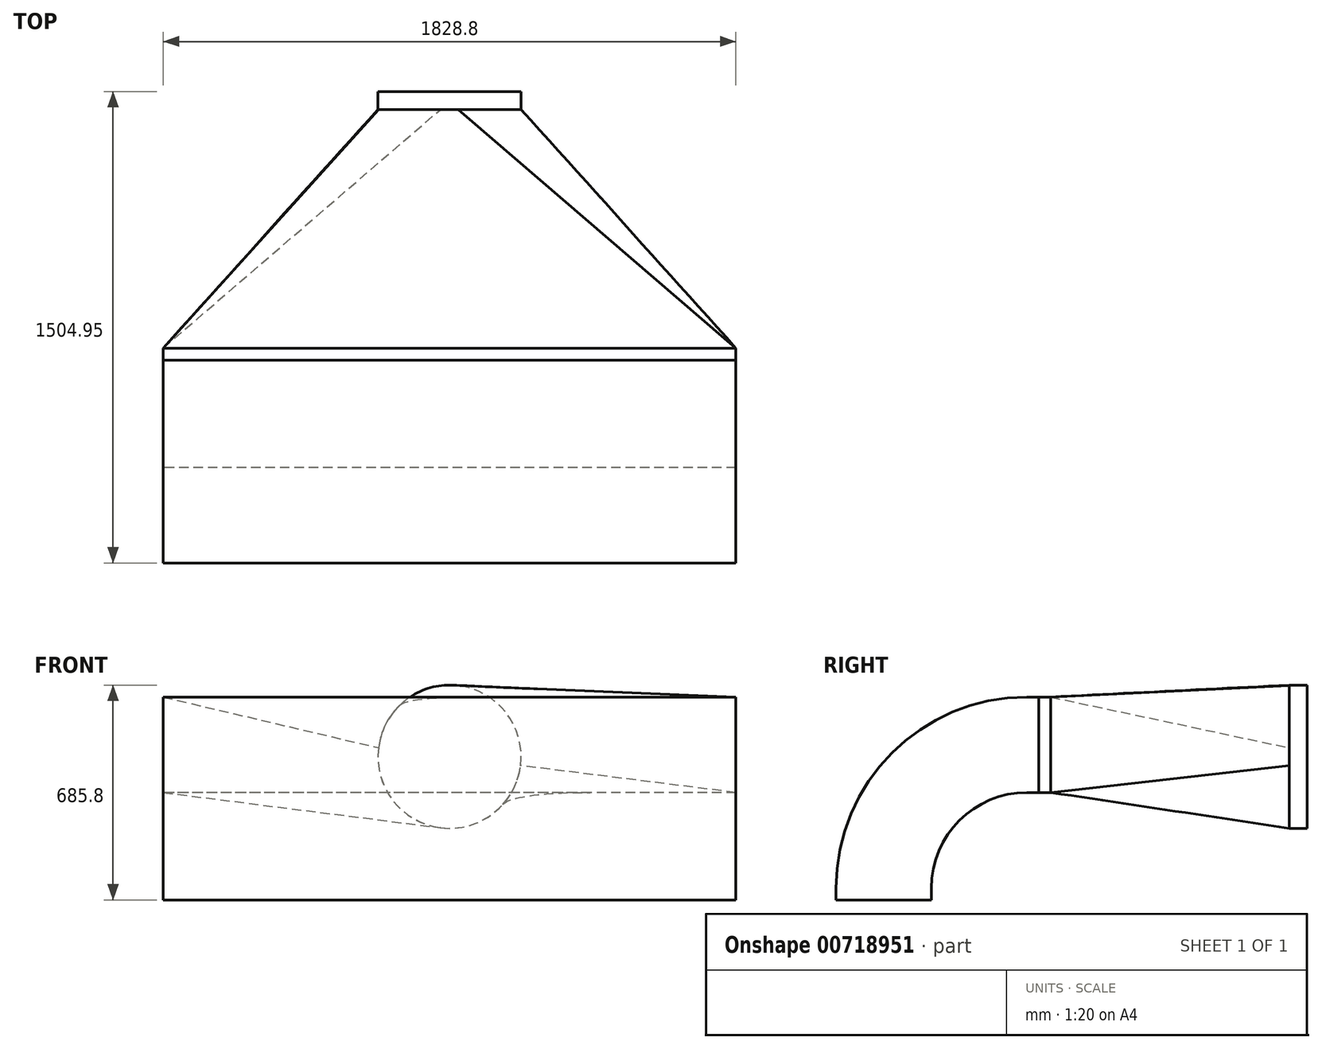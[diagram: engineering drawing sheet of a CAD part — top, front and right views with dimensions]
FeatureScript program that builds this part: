
annotation { "Feature Type Name" : "Feature", "Feature Type Description" : "" }
export const myFeature = defineFeature(function(context is Context, id is Id, definition is map)
    precondition{}
    {
        {
            var Q0;
            Q0=qCreatedBy(makeId("Top.planeOp"),FACE);
            var sketch = newSketch(context, id + "F0", { "sketchPlane" : qUnion([Q0])});
            skLineSegment(sketch, "E0.bottom", {"start": v(914.4, 152.4) * mm, "end": v(-914.4, 152.4) * mm});
            skLineSegment(sketch, "E0.top", {"start": v(914.4, -152.4) * mm, "end": v(-914.4, -152.4) * mm});
            skLineSegment(sketch, "E0.left", {"start": v(914.4, 152.4) * mm, "end": v(914.4, -152.4) * mm});
            skLineSegment(sketch, "E0.right", {"start": v(-914.4, 152.4) * mm, "end": v(-914.4, -152.4) * mm});
            skPoint(sketch, "E0.middle", {"position": v(0, 0) * mm});
            skSolve(sketch);
        }
        {
            var Q0;
            Q0=makeQuery(id+"F0.imprint","IMPRINT",FACE,{"disambiguationData":[TD([[makeQuery(id+"F0.imprint","IMPRINT",EDGE,{"derivedFrom":sQuery(id+"F0.wireOp",EDGE,"E0.bottom")}),1.0]])]});
            extrude(context, id + "F1", {"entities" : qUnion([Q0]), "depth" : 38.1 * mm, "offsetDistance" : 25.4 * mm});
        }
        {
            var Q0;
            Q0=makeQuery(id+"F1.opExtrude","CAP_FACE",FACE,{"disambiguationData":[OSD([sQuery(id+"F0.wireOp",EDGE,"E0.bottom"),sQuery(id+"F0.wireOp",EDGE,"E0.top"),sQuery(id+"F0.wireOp",EDGE,"E0.left"),sQuery(id+"F0.wireOp",EDGE,"E0.right")])],"isStart":false});
            var sketch = newSketch(context, id + "F2", { "sketchPlane" : qUnion([Q0])});
            skLineSegment(sketch, "E1", {"start": v(0, 0) * mm, "end": v(0, 457.2) * mm, "construction": true});
            skPoint(sketch, "E1.endSnap0", {"position": v(0, 152.4) * mm});
            skLineSegment(sketch, "E2", {"start": v(0, 457.2) * mm, "end": v(-206.41, 457.2) * mm});
            skSolve(sketch);
        }
        {
            var Q0;
            Q0=makeQuery(id+"F2.imprint","IMPRINT",FACE,{"disambiguationData":[TD([[makeQuery(id+"F2.imprint","IMPRINT",EDGE,{"derivedFrom":makeQuery(id+"F1.opExtrude","CAP_EDGE",EDGE,{"disambiguationData":[OSD([sQuery(id+"F0.wireOp",EDGE,"E0.bottom")])],"isStart":false})}),1.0]])]});
            var Q1;
            Q1=sQuery(id+"F2.wireOp",EDGE,"E2");
            revolve(context, id + "F3", {"operationType" : NewBodyOperationType.ADD, "surfaceOperationType" : NewSurfaceOperationType.NEW, "entities" : qUnion([Q0]), "axis" : qUnion([Q1]), "revolveType" : RevolveType.ONE_DIRECTION, "angle" : 90 * degree});
        }
        {
            var Q0;
            Q0=makeQuery(id+"F3.opRevolve","CAP_FACE",FACE,{"disambiguationData":[OSD([sQuery(id+"F0.wireOp",EDGE,"E0.bottom"),sQuery(id+"F0.wireOp",EDGE,"E0.top"),sQuery(id+"F0.wireOp",EDGE,"E0.left"),sQuery(id+"F0.wireOp",EDGE,"E0.right")])],"isStart":false});
            extrude(context, id + "F4", {"entities" : qUnion([Q0]), "operationType" : NewBodyOperationType.ADD, "depth" : 38.1 * mm, "offsetDistance" : 25.4 * mm});
        }
        {
            var Q0;
            Q0=makeQuery(id+"F4.opExtrude","CAP_FACE",FACE,{"disambiguationData":[OSD([sQuery(id+"F0.wireOp",EDGE,"E0.bottom"),sQuery(id+"F0.wireOp",EDGE,"E0.top"),sQuery(id+"F0.wireOp",EDGE,"E0.left"),sQuery(id+"F0.wireOp",EDGE,"E0.right")])],"isStart":false});
            var sketch = newSketch(context, id + "F5", { "sketchPlane" : qUnion([Q0])});
            skLineSegment(sketch, "E3.bottom", {"start": v(-914.4, 647.7) * mm, "end": v(914.4, 647.7) * mm});
            skLineSegment(sketch, "E3.top", {"start": v(-914.4, 342.9) * mm, "end": v(914.4, 342.9) * mm});
            skLineSegment(sketch, "E3.left", {"start": v(-914.4, 647.7) * mm, "end": v(-914.4, 342.9) * mm});
            skLineSegment(sketch, "E3.right", {"start": v(914.4, 647.7) * mm, "end": v(914.4, 342.9) * mm});
            skSolve(sketch);
        }
        {
            var Q0;
            Q0 = qSketchRegion(id + "F5", true);
            extrude(context, id + "F6", {"entities" : qUnion([Q0]), "depth" : 38.1 * mm, "offsetDistance" : 25.4 * mm});
        }
        {
            var Q0;
            Q0=makeQuery(id+"F6.opExtrude","CAP_FACE",FACE,{"disambiguationData":[OSD([sQuery(id+"F5.wireOp",EDGE,"E3.bottom"),sQuery(id+"F5.wireOp",EDGE,"E3.top"),sQuery(id+"F5.wireOp",EDGE,"E3.left"),sQuery(id+"F5.wireOp",EDGE,"E3.right")])],"isStart":false});
            cPlane(context, id + "F7", {"entities" : qUnion([Q0]), "cplaneType" : CPlaneType.OFFSET, "offset" : 762 * mm, "width" : 152.4 * mm, "height" : 152.4 * mm});
        }
        {
            var Q0;
            Q0=qCreatedBy(id+"F7.planeOp",FACE);
            var sketch = newSketch(context, id + "F8", { "sketchPlane" : qUnion([Q0])});
            skLineSegment(sketch, "E4", {"start": v(0, 0) * mm, "end": v(0, 457.2) * mm, "construction": true});
            skCircle(sketch, "E5", {"center": v(0, 457.2) * mm, "radius": 228.6 * mm});
            skSolve(sketch);
        }
        {
            var Q1;
            Q1=makeQuery(id+"F6.opExtrude","CAP_FACE",FACE,{"disambiguationData":[OSD([sQuery(id+"F5.wireOp",EDGE,"E3.bottom"),sQuery(id+"F5.wireOp",EDGE,"E3.top"),sQuery(id+"F5.wireOp",EDGE,"E3.left"),sQuery(id+"F5.wireOp",EDGE,"E3.right")])],"isStart":false});
            var Q2;
            Q2=makeQuery(id+"F8.imprint","IMPRINT",FACE,{"disambiguationData":[TD([[makeQuery(id+"F8.imprint","IMPRINT",EDGE,{"derivedFrom":sQuery(id+"F8.wireOp",EDGE,"E5")}),1.0]])]});
            loft(context, id + "F9", {"operationType" : NewBodyOperationType.ADD, "sheetProfilesArray" : [{ "sheetProfileEntities" : qUnion([Q1]) }, { "sheetProfileEntities" : qUnion([Q2]) }]});
        }
        {
            var Q0;
            Q0=makeQuery(id+"F9.opLoft","CAP_FACE",FACE,{"disambiguationData":[OSD([makeQuery(id+"F8.imprint","IMPRINT",FACE,{"disambiguationData":[TD([[makeQuery(id+"F8.imprint","IMPRINT",EDGE,{"derivedFrom":sQuery(id+"F8.wireOp",EDGE,"E5")}),1.0]])]})])],"isStart":true});
            extrude(context, id + "F10", {"entities" : qUnion([Q0]), "operationType" : NewBodyOperationType.ADD, "depth" : 57.15 * mm, "offsetDistance" : 25.4 * mm});
        }
    });
